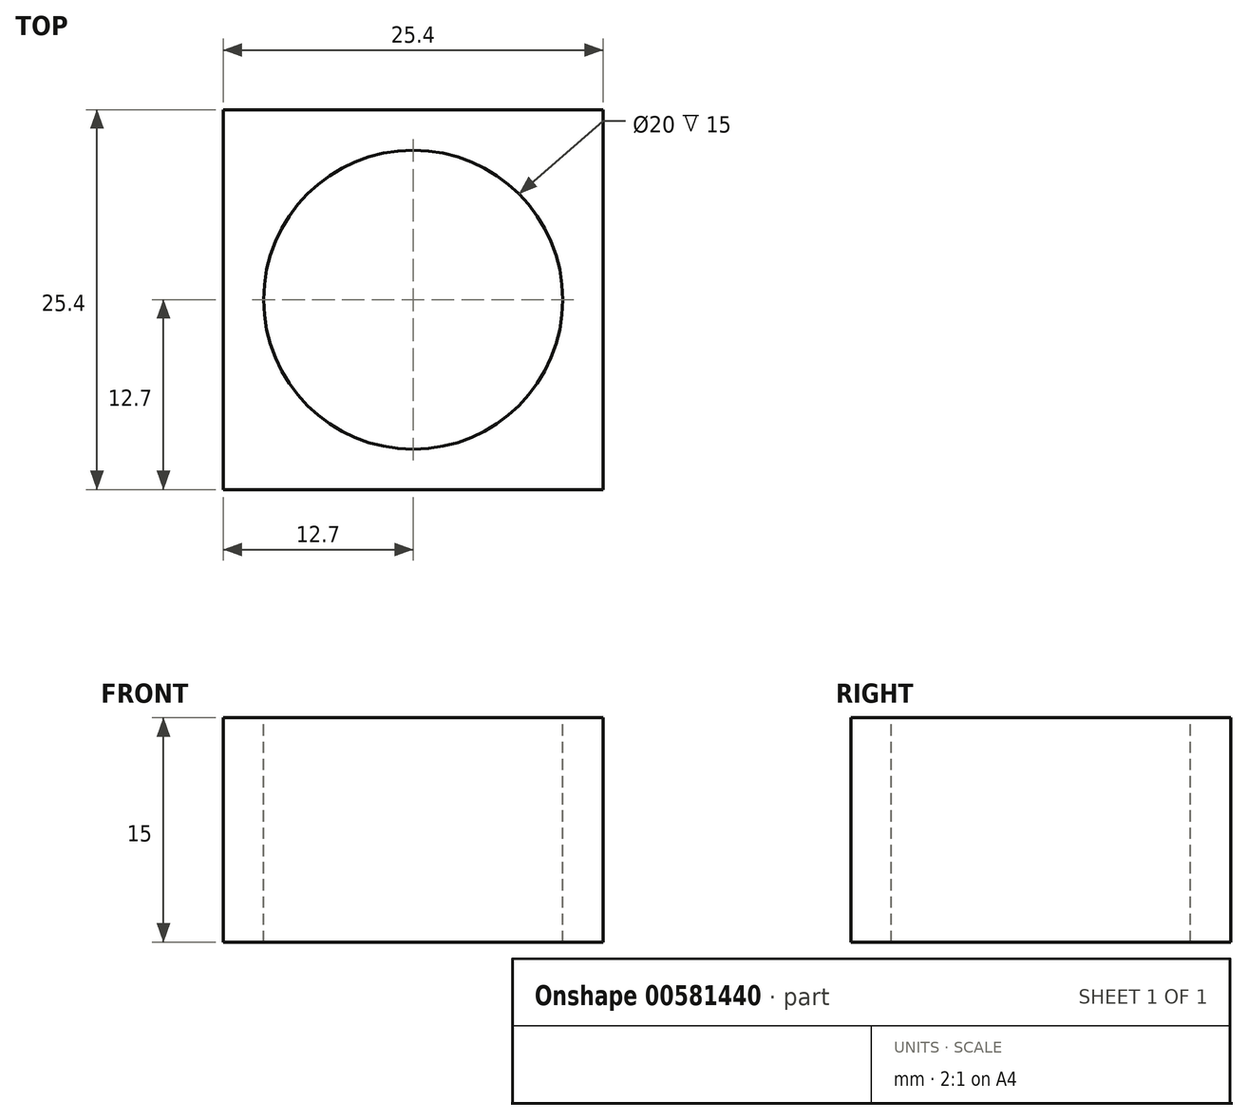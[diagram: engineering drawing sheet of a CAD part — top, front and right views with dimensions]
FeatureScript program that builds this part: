
annotation { "Feature Type Name" : "Feature", "Feature Type Description" : "" }
export const myFeature = defineFeature(function(context is Context, id is Id, definition is map)
    precondition{}
    {
        {
            var Q0;
            Q0=qCreatedBy(makeId("Top.planeOp"),FACE);
            var sketch = newSketch(context, id + "F0", { "sketchPlane" : qUnion([Q0])});
            skLineSegment(sketch, "E0.bottom", {"start": v(-12.7, 12.7) * mm, "end": v(12.7, 12.7) * mm});
            skLineSegment(sketch, "E0.top", {"start": v(-12.7, -12.7) * mm, "end": v(12.7, -12.7) * mm});
            skLineSegment(sketch, "E0.left", {"start": v(-12.7, 12.7) * mm, "end": v(-12.7, -12.7) * mm});
            skLineSegment(sketch, "E0.right", {"start": v(12.7, 12.7) * mm, "end": v(12.7, -12.7) * mm});
            skSolve(sketch);
        }
        {
            var Q0;
            Q0=makeQuery(id+"F0.imprint","IMPRINT",FACE,{"disambiguationData":[TD([[makeQuery(id+"F0.imprint","IMPRINT",EDGE,{"derivedFrom":sQuery(id+"F0.wireOp",EDGE,"E0.bottom")}),-1.0]])]});
            extrude(context, id + "F1", {"entities" : qUnion([Q0]), "depth" : 15 * mm, "offsetDistance" : 25 * mm});
        }
        {
            var Q0;
            Q0=makeQuery(id+"F1.opExtrude","CAP_FACE",FACE,{"disambiguationData":[OSD([sQuery(id+"F0.wireOp",EDGE,"E0.bottom"),sQuery(id+"F0.wireOp",EDGE,"E0.top"),sQuery(id+"F0.wireOp",EDGE,"E0.left"),sQuery(id+"F0.wireOp",EDGE,"E0.right")])],"isStart":false});
            var sketch = newSketch(context, id + "F2", { "sketchPlane" : qUnion([Q0])});
            skCircle(sketch, "E1", {"center": v(0, 0) * mm, "radius": 10 * mm});
            skSolve(sketch);
        }
        {
            var Q0;
            Q0=makeQuery(id+"F2.imprint","IMPRINT",FACE,{"disambiguationData":[TD([[makeQuery(id+"F2.imprint","IMPRINT",EDGE,{"derivedFrom":sQuery(id+"F2.wireOp",EDGE,"E1")}),1.0]])]});
            extrude(context, id + "F3", {"entities" : qUnion([Q0]), "operationType" : NewBodyOperationType.REMOVE, "endBound" : BoundingType.UP_TO_NEXT, "oppositeDirection" : true, "depth" : 25 * mm, "offsetDistance" : 25 * mm});
        }
    });
